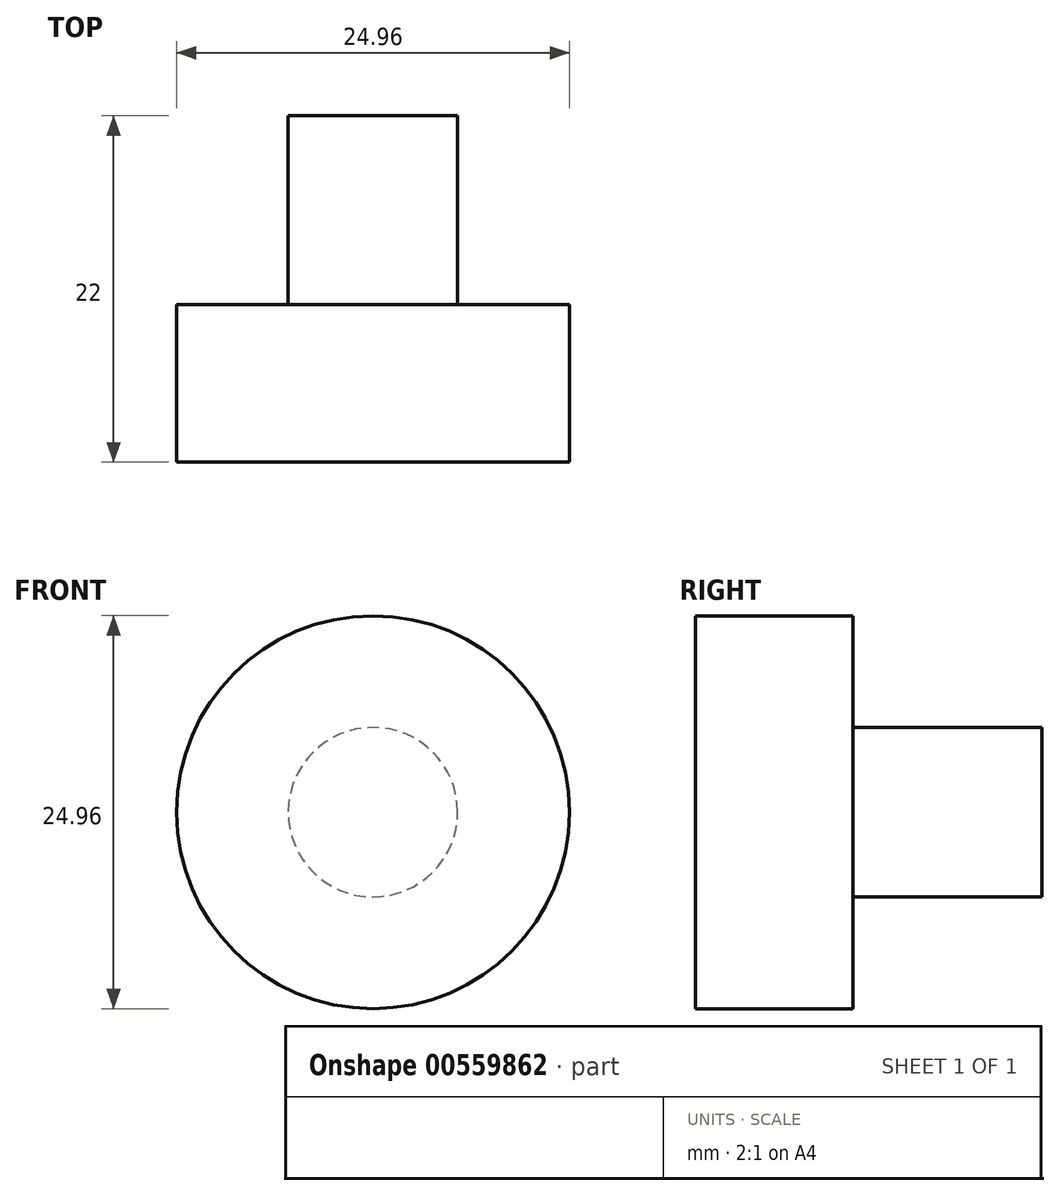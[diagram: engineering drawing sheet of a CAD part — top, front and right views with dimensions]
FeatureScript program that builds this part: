
annotation { "Feature Type Name" : "Feature", "Feature Type Description" : "" }
export const myFeature = defineFeature(function(context is Context, id is Id, definition is map)
    precondition{}
    {
        {
            var Q0;
            Q0=qCreatedBy(makeId("Front.planeOp"),FACE);
            var sketch = newSketch(context, id + "F0", { "sketchPlane" : qUnion([Q0])});
            skCircle(sketch, "E0", {"center": v(0, 0) * mm, "radius": 12.48 * mm});
            skSolve(sketch);
        }
        {
            var Q0;
            Q0=makeQuery(id+"F0.imprint","IMPRINT",FACE,{"disambiguationData":[TD([[makeQuery(id+"F0.imprint","IMPRINT",EDGE,{"derivedFrom":sQuery(id+"F0.wireOp",EDGE,"E0")}),1.0]])]});
            extrude(context, id + "F1", {"entities" : qUnion([Q0]), "depth" : 10 * mm, "offsetDistance" : 25 * mm});
        }
        {
            var Q0;
            Q0=makeQuery(id+"F1.opExtrude","CAP_FACE",FACE,{"disambiguationData":[OSD([sQuery(id+"F0.wireOp",EDGE,"E0")])],"isStart":true});
            var sketch = newSketch(context, id + "F2", { "sketchPlane" : qUnion([Q0])});
            skCircle(sketch, "E1", {"center": v(0, 0) * mm, "radius": 5.38 * mm});
            skSolve(sketch);
        }
        {
            var Q0;
            Q0=makeQuery(id+"F2.imprint","IMPRINT",FACE,{"disambiguationData":[TD([[makeQuery(id+"F2.imprint","IMPRINT",EDGE,{"derivedFrom":sQuery(id+"F2.wireOp",EDGE,"E1")}),1.0]])]});
            extrude(context, id + "F3", {"entities" : qUnion([Q0]), "operationType" : NewBodyOperationType.ADD, "depth" : 12 * mm, "offsetDistance" : 25 * mm});
        }
    });
